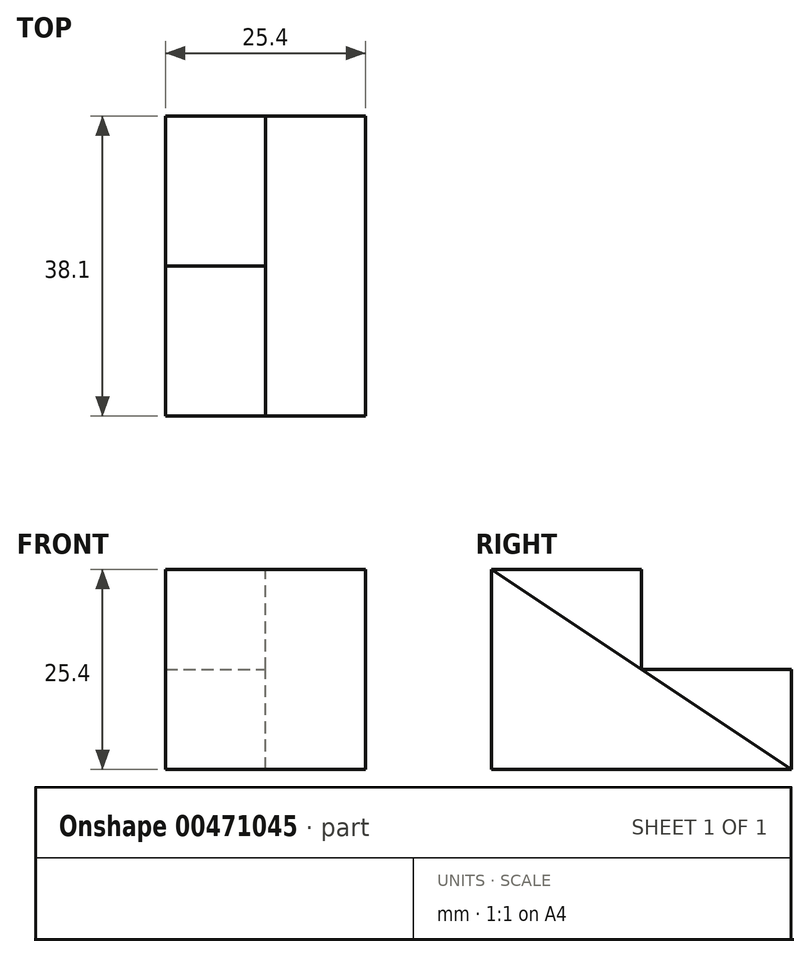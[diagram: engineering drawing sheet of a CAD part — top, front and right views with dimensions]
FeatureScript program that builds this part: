
annotation { "Feature Type Name" : "Feature", "Feature Type Description" : "" }
export const myFeature = defineFeature(function(context is Context, id is Id, definition is map)
    precondition{}
    {
        {
            var Q0;
            Q0=qCreatedBy(makeId("Right.planeOp"),FACE);
            var sketch = newSketch(context, id + "F0", { "sketchPlane" : qUnion([Q0])});
            skLineSegment(sketch, "E0.bottom", {"start": v(0, 0) * mm, "end": v(-38.1, 0) * mm});
            skLineSegment(sketch, "E0.top", {"start": v(0, 25.4) * mm, "end": v(-38.1, 25.4) * mm});
            skLineSegment(sketch, "E0.left", {"start": v(0, 0) * mm, "end": v(0, 25.4) * mm});
            skLineSegment(sketch, "E0.right", {"start": v(-38.1, 0) * mm, "end": v(-38.1, 25.4) * mm});
            skSolve(sketch);
        }
        {
            var Q0;
            Q0=makeQuery(id+"F0.imprint","IMPRINT",FACE,{"disambiguationData":[TD([[makeQuery(id+"F0.imprint","IMPRINT",EDGE,{"derivedFrom":sQuery(id+"F0.wireOp",EDGE,"E0.bottom")}),-1.0]])]});
            extrude(context, id + "F1", {"entities" : qUnion([Q0]), "depth" : 12.7 * mm});
        }
        {
            var Q0;
            Q0=makeQuery(id+"F1.opExtrude","SWEPT_EDGE",EDGE,{"disambiguationData":[OSD([sQuery(id+"F0.wireOp",EDGE,"E0.top"),sQuery(id+"F0.wireOp",EDGE,"E0.left")])]});
            chamfer(context, id + "F2", {"entities" : qUnion([Q0]), "chamferType" : ChamferType.TWO_OFFSETS, "width1" : 38.1 * mm, "oppositeDirection" : false, "width2" : 25.4 * mm, "tangentPropagation" : true});
        }
        {
            var Q0;
            Q0=qCreatedBy(makeId("Right.planeOp"),FACE);
            var sketch = newSketch(context, id + "F3", { "sketchPlane" : qUnion([Q0])});
            skLineSegment(sketch, "E1.bottom", {"start": v(0, 0) * mm, "end": v(-38.1, 0) * mm});
            skLineSegment(sketch, "E1.top", {"start": v(-19.05, 25.4) * mm, "end": v(-38.1, 25.4) * mm});
            skLineSegment(sketch, "E1.left", {"start": v(0, 0) * mm, "end": v(0, 12.7) * mm});
            skLineSegment(sketch, "E1.right", {"start": v(-38.1, 0) * mm, "end": v(-38.1, 25.4) * mm});
            skLineSegment(sketch, "E2.top", {"start": v(0, 12.7) * mm, "end": v(-19.05, 12.7) * mm});
            skLineSegment(sketch, "E2.right", {"start": v(-19.05, 25.4) * mm, "end": v(-19.05, 12.7) * mm});
            skSolve(sketch);
        }
        {
            var Q0;
            Q0 = qSketchRegion(id + "F3", true);
            extrude(context, id + "F4", {"entities" : qUnion([Q0]), "operationType" : NewBodyOperationType.ADD, "oppositeDirection" : true, "depth" : 12.7 * mm});
        }
    });
